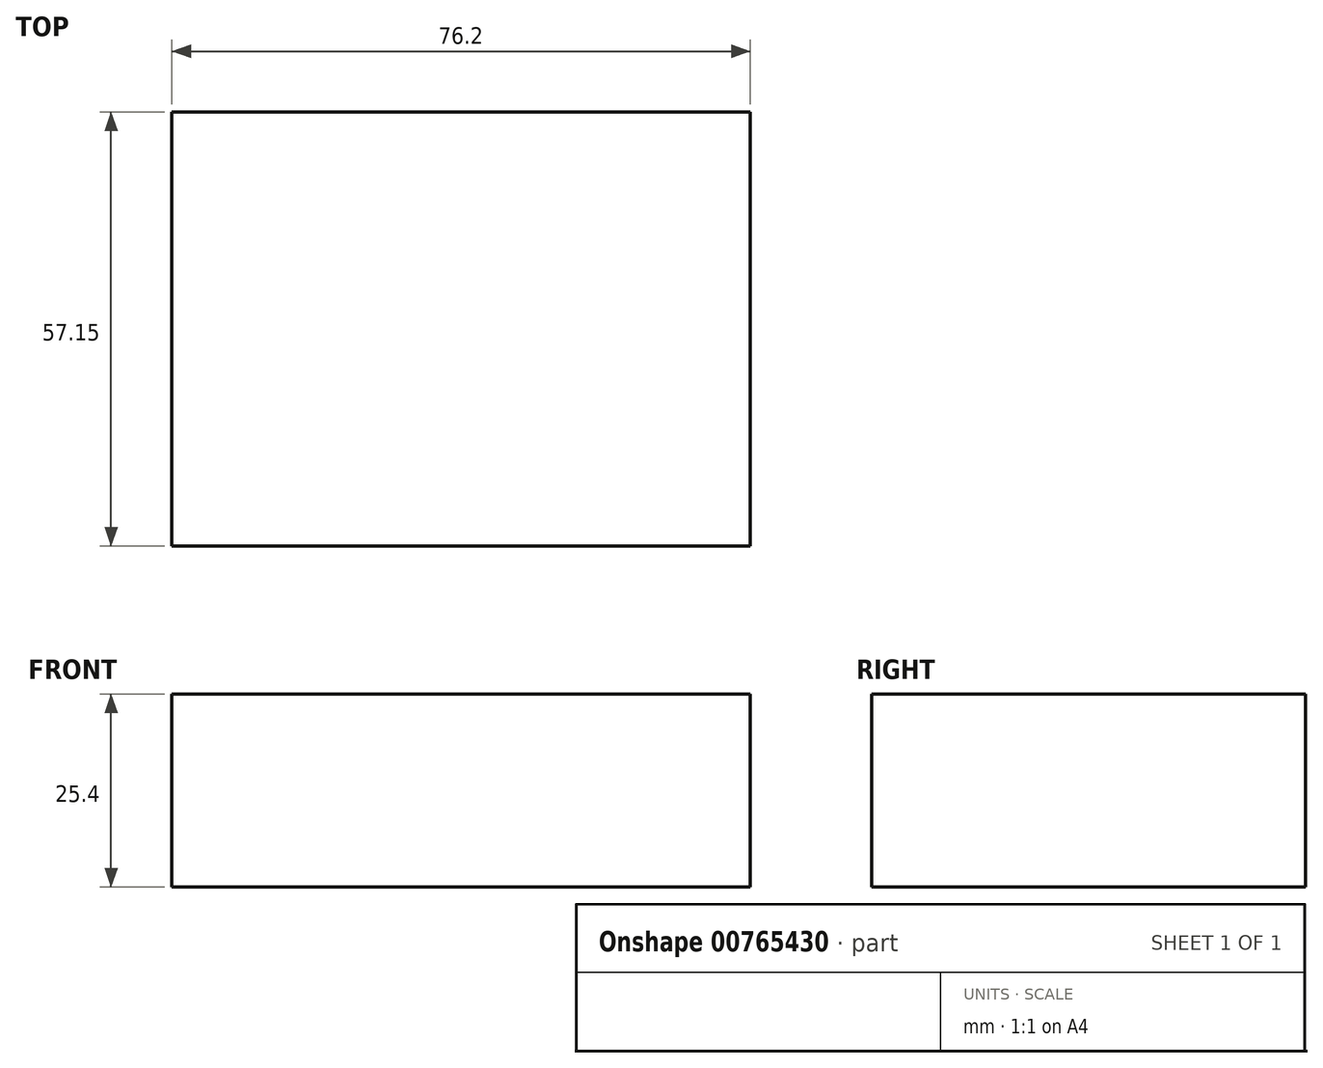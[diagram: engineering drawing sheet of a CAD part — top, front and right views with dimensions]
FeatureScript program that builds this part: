
annotation { "Feature Type Name" : "Feature", "Feature Type Description" : "" }
export const myFeature = defineFeature(function(context is Context, id is Id, definition is map)
    precondition{}
    {
        {
            var Q0;
            Q0=qCreatedBy(makeId("Top.planeOp"),FACE);
            var sketch = newSketch(context, id + "F0", { "sketchPlane" : qUnion([Q0])});
            skLineSegment(sketch, "E0.bottom", {"start": v(0, 0) * mm, "end": v(-76.2, 0) * mm});
            skLineSegment(sketch, "E0.top", {"start": v(0, -57.15) * mm, "end": v(-76.2, -57.15) * mm});
            skLineSegment(sketch, "E0.left", {"start": v(0, 0) * mm, "end": v(0, -57.15) * mm});
            skLineSegment(sketch, "E0.right", {"start": v(-76.2, 0) * mm, "end": v(-76.2, -57.15) * mm});
            skSolve(sketch);
        }
        {
            var Q0;
            Q0=makeQuery(id+"F0.imprint","IMPRINT",FACE,{"disambiguationData":[TD([[makeQuery(id+"F0.imprint","IMPRINT",EDGE,{"derivedFrom":sQuery(id+"F0.wireOp",EDGE,"E0.bottom")}),1.0]])]});
            extrude(context, id + "F1", {"entities" : qUnion([Q0]), "depth" : 25.4 * mm, "offsetDistance" : 25.4 * mm});
        }
    });
